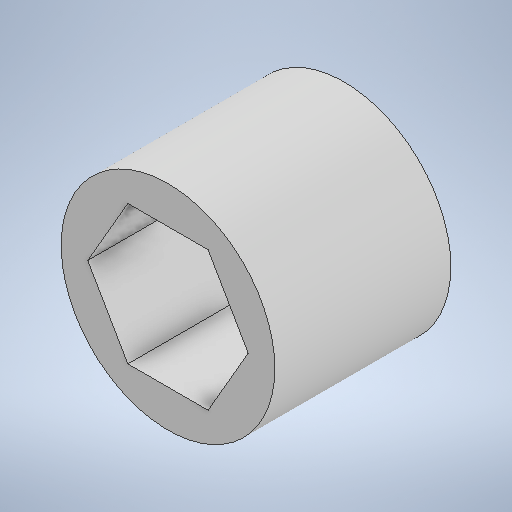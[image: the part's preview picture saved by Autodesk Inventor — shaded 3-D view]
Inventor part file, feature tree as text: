
AUTODESK INVENTOR PART (.ipt)
format: ipt  version: 2025.1 (Build 291241020, 241B)  size: 218,624 bytes
history: native  units: in
note: dims shown in document units (in); Inventor stores cm internally (conversion verified against a paired STEP export)
features: extrude x1, sketch x1
ambient origin geometry x8: Origin, YZ Plane, XZ Plane, XY Plane, X Axis, Y Axis, Z Axis, Center Point
bodies: Solid1 (feature_tree)
feature tree (2):
  extrude  "Extrusion1"  Depth=0.4998in
  sketch  "Sketch1"  dims[d0=0.768in d1=0.4998in d2=0.633in d3=0.0in]
